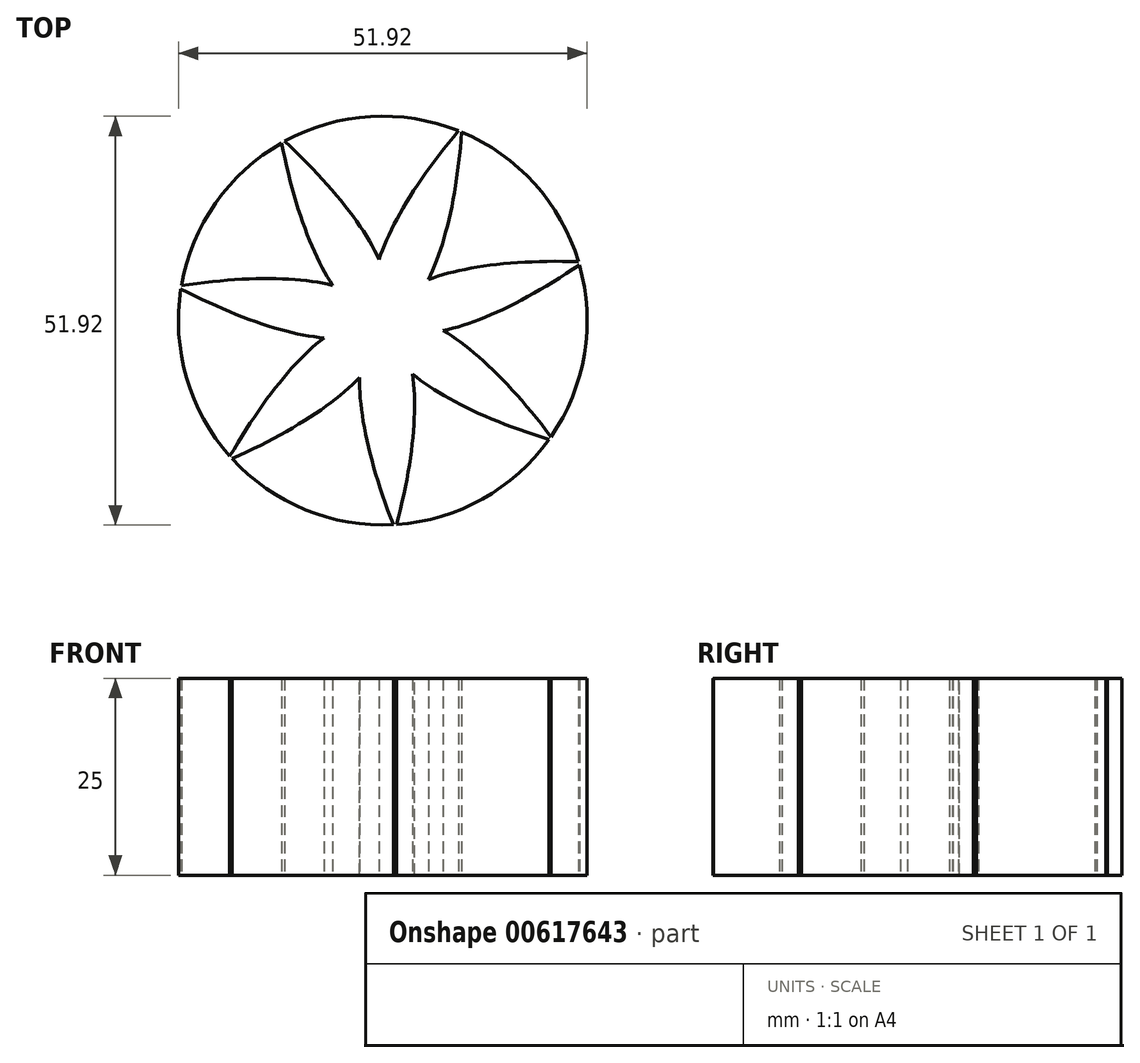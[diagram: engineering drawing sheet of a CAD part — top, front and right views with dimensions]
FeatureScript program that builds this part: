
annotation { "Feature Type Name" : "Feature", "Feature Type Description" : "" }
export const myFeature = defineFeature(function(context is Context, id is Id, definition is map)
    precondition{}
    {
        {
            var Q0;
            Q0=qCreatedBy(makeId("Top.planeOp"),FACE);
            var sketch = newSketch(context, id + "F0", { "sketchPlane" : qUnion([Q0])});
            skEllipse(sketch, "E0", {"center": v(-30.78, 21.65) * mm, "majorRadius": 37.63 * mm, "minorRadius": 12.4 * mm, "majorAxis": v(0.82, -0.58)});
            skEllipse(sketch, "E1.1.0", {"center": v(-36.12, -10.57) * mm, "majorRadius": 37.63 * mm, "minorRadius": 12.4 * mm, "majorAxis": v(0.96, 0.28)});
            skEllipse(sketch, "E1.2.0", {"center": v(-14.25, -34.83) * mm, "majorRadius": 37.63 * mm, "minorRadius": 12.4 * mm, "majorAxis": v(0.38, 0.93)});
            skEllipse(sketch, "E1.3.0", {"center": v(18.34, -32.86) * mm, "majorRadius": 37.63 * mm, "minorRadius": 12.4 * mm, "majorAxis": v(-0.49, 0.87)});
            skEllipse(sketch, "E1.4.0", {"center": v(37.13, -6.15) * mm, "majorRadius": 37.63 * mm, "minorRadius": 12.4 * mm, "majorAxis": v(-0.99, 0.16)});
            skEllipse(sketch, "E1.5.0", {"center": v(27.95, 25.2) * mm, "majorRadius": 37.63 * mm, "minorRadius": 12.4 * mm, "majorAxis": v(-0.74, -0.67)});
            skEllipse(sketch, "E1.6.0", {"center": v(-2.27, 37.56) * mm, "majorRadius": 37.63 * mm, "minorRadius": 12.4 * mm, "majorAxis": v(0.06, -1)});
            skPoint(sketch, "E1.center", {"position": v(0, 0) * mm});
            skCircle(sketch, "E2", {"center": v(0, 0) * mm, "radius": 25.96 * mm});
            skCircle(sketch, "E3", {"center": v(0, 0) * mm, "radius": 19.78 * mm});
            skSolve(sketch);
        }
        {
            var Q0;
            {var subQ0=sQuery(id+"F0.wireOp",EDGE,"E3");var subQ1=sQuery(id+"F0.wireOp",EDGE,"E1.1.0");var subQ2=makeQuery(id+"F0.imprint","INTERSECT",VERTEX,{"disambiguationData":[OD(0.0)],"derivedFrom":[subQ1,subQ0]});Q0=makeQuery(id+"F0.imprint","IMPRINT",FACE,{"disambiguationData":[TD([[makeQuery(id+"F0.imprint","IMPRINT",EDGE,{"disambiguationData":[TD([[subQ2,-1.0]])],"derivedFrom":subQ1}),-1.0]])]});}
            var Q1;
            {var subQ0=sQuery(id+"F0.wireOp",EDGE,"E2");var subQ1=sQuery(id+"F0.wireOp",EDGE,"E0");var subQ2=makeQuery(id+"F0.imprint","INTERSECT",VERTEX,{"disambiguationData":[OD(1.0)],"derivedFrom":[subQ1,subQ0]});Q1=makeQuery(id+"F0.imprint","IMPRINT",FACE,{"disambiguationData":[TD([[makeQuery(id+"F0.imprint","IMPRINT",EDGE,{"disambiguationData":[TD([[subQ2,-1.0]])],"derivedFrom":subQ1}),-1.0]])]});}
            var Q2;
            {var subQ0=sQuery(id+"F0.wireOp",EDGE,"E2");var subQ1=sQuery(id+"F0.wireOp",EDGE,"E1.1.0");var subQ2=makeQuery(id+"F0.imprint","INTERSECT",VERTEX,{"disambiguationData":[OD(1.0)],"derivedFrom":[subQ1,subQ0]});Q2=makeQuery(id+"F0.imprint","IMPRINT",FACE,{"disambiguationData":[TD([[makeQuery(id+"F0.imprint","IMPRINT",EDGE,{"disambiguationData":[TD([[subQ2,-1.0]])],"derivedFrom":subQ1}),-1.0]])]});}
            var Q3;
            {var subQ0=sQuery(id+"F0.wireOp",EDGE,"E2");var subQ1=sQuery(id+"F0.wireOp",EDGE,"E1.2.0");var subQ2=makeQuery(id+"F0.imprint","INTERSECT",VERTEX,{"disambiguationData":[OD(1.0)],"derivedFrom":[subQ1,subQ0]});Q3=makeQuery(id+"F0.imprint","IMPRINT",FACE,{"disambiguationData":[TD([[makeQuery(id+"F0.imprint","IMPRINT",EDGE,{"disambiguationData":[TD([[subQ2,-1.0]])],"derivedFrom":subQ1}),-1.0]])]});}
            var Q4;
            {var subQ0=sQuery(id+"F0.wireOp",EDGE,"E2");var subQ1=sQuery(id+"F0.wireOp",EDGE,"E1.3.0");var subQ2=makeQuery(id+"F0.imprint","INTERSECT",VERTEX,{"disambiguationData":[OD(1.0)],"derivedFrom":[subQ1,subQ0]});Q4=makeQuery(id+"F0.imprint","IMPRINT",FACE,{"disambiguationData":[TD([[makeQuery(id+"F0.imprint","IMPRINT",EDGE,{"disambiguationData":[TD([[subQ2,-1.0]])],"derivedFrom":subQ1}),-1.0]])]});}
            var Q5;
            {var subQ0=sQuery(id+"F0.wireOp",EDGE,"E2");var subQ1=sQuery(id+"F0.wireOp",EDGE,"E1.4.0");var subQ2=makeQuery(id+"F0.imprint","INTERSECT",VERTEX,{"disambiguationData":[OD(1.0)],"derivedFrom":[subQ1,subQ0]});Q5=makeQuery(id+"F0.imprint","IMPRINT",FACE,{"disambiguationData":[TD([[makeQuery(id+"F0.imprint","IMPRINT",EDGE,{"disambiguationData":[TD([[subQ2,-1.0]])],"derivedFrom":subQ1}),-1.0]])]});}
            var Q6;
            {var subQ0=sQuery(id+"F0.wireOp",EDGE,"E3");var subQ1=sQuery(id+"F0.wireOp",EDGE,"E0");var subQ2=makeQuery(id+"F0.imprint","INTERSECT",VERTEX,{"disambiguationData":[OD(0.0)],"derivedFrom":[subQ1,subQ0]});Q6=makeQuery(id+"F0.imprint","IMPRINT",FACE,{"disambiguationData":[TD([[makeQuery(id+"F0.imprint","IMPRINT",EDGE,{"disambiguationData":[TD([[subQ2,-1.0]])],"derivedFrom":subQ1}),-1.0]])]});}
            var Q7;
            {var subQ0=sQuery(id+"F0.wireOp",EDGE,"E1.6.0");var subQ1=sQuery(id+"F0.wireOp",EDGE,"E1.1.0");var subQ2=makeQuery(id+"F0.imprint","INTERSECT",VERTEX,{"derivedFrom":[subQ1,subQ0]});Q7=makeQuery(id+"F0.imprint","IMPRINT",FACE,{"disambiguationData":[TD([[makeQuery(id+"F0.imprint","IMPRINT",EDGE,{"disambiguationData":[TD([[subQ2,-1.0]])],"derivedFrom":subQ1}),-1.0]])]});}
            var Q8;
            {var subQ0=sQuery(id+"F0.wireOp",EDGE,"E3");var subQ1=sQuery(id+"F0.wireOp",EDGE,"E0");var subQ2=makeQuery(id+"F0.imprint","INTERSECT",VERTEX,{"disambiguationData":[OD(1.0)],"derivedFrom":[subQ1,subQ0]});Q8=makeQuery(id+"F0.imprint","IMPRINT",FACE,{"disambiguationData":[TD([[makeQuery(id+"F0.imprint","IMPRINT",EDGE,{"disambiguationData":[TD([[subQ2,-1.0]])],"derivedFrom":subQ1}),-1.0]])]});}
            var Q9;
            {var subQ0=sQuery(id+"F0.wireOp",EDGE,"E3");var subQ1=sQuery(id+"F0.wireOp",EDGE,"E1.1.0");var subQ2=makeQuery(id+"F0.imprint","INTERSECT",VERTEX,{"disambiguationData":[OD(1.0)],"derivedFrom":[subQ1,subQ0]});Q9=makeQuery(id+"F0.imprint","IMPRINT",FACE,{"disambiguationData":[TD([[makeQuery(id+"F0.imprint","IMPRINT",EDGE,{"disambiguationData":[TD([[subQ2,-1.0]])],"derivedFrom":subQ1}),-1.0]])]});}
            var Q10;
            {var subQ0=sQuery(id+"F0.wireOp",EDGE,"E3");var subQ1=sQuery(id+"F0.wireOp",EDGE,"E1.2.0");var subQ2=makeQuery(id+"F0.imprint","INTERSECT",VERTEX,{"disambiguationData":[OD(1.0)],"derivedFrom":[subQ1,subQ0]});Q10=makeQuery(id+"F0.imprint","IMPRINT",FACE,{"disambiguationData":[TD([[makeQuery(id+"F0.imprint","IMPRINT",EDGE,{"disambiguationData":[TD([[subQ2,-1.0]])],"derivedFrom":subQ1}),-1.0]])]});}
            var Q11;
            {var subQ0=sQuery(id+"F0.wireOp",EDGE,"E3");var subQ1=sQuery(id+"F0.wireOp",EDGE,"E1.3.0");var subQ2=makeQuery(id+"F0.imprint","INTERSECT",VERTEX,{"disambiguationData":[OD(1.0)],"derivedFrom":[subQ1,subQ0]});Q11=makeQuery(id+"F0.imprint","IMPRINT",FACE,{"disambiguationData":[TD([[makeQuery(id+"F0.imprint","IMPRINT",EDGE,{"disambiguationData":[TD([[subQ2,-1.0]])],"derivedFrom":subQ1}),-1.0]])]});}
            var Q12;
            {var subQ0=sQuery(id+"F0.wireOp",EDGE,"E3");var subQ1=sQuery(id+"F0.wireOp",EDGE,"E1.4.0");var subQ2=makeQuery(id+"F0.imprint","INTERSECT",VERTEX,{"disambiguationData":[OD(1.0)],"derivedFrom":[subQ1,subQ0]});Q12=makeQuery(id+"F0.imprint","IMPRINT",FACE,{"disambiguationData":[TD([[makeQuery(id+"F0.imprint","IMPRINT",EDGE,{"disambiguationData":[TD([[subQ2,-1.0]])],"derivedFrom":subQ1}),-1.0]])]});}
            var Q13;
            {var subQ0=sQuery(id+"F0.wireOp",EDGE,"E1.5.0");var subQ1=sQuery(id+"F0.wireOp",EDGE,"E0");var subQ2=makeQuery(id+"F0.imprint","INTERSECT",VERTEX,{"derivedFrom":[subQ1,subQ0]});Q13=makeQuery(id+"F0.imprint","IMPRINT",FACE,{"disambiguationData":[TD([[makeQuery(id+"F0.imprint","IMPRINT",EDGE,{"disambiguationData":[TD([[subQ2,-1.0]])],"derivedFrom":subQ1}),-1.0]])]});}
            extrude(context, id + "F1", {"entities" : qUnion([Q0, Q1, Q2, Q3, Q4, Q5, Q6, Q7, Q8, Q9, Q10, Q11, Q12, Q13]), "depth" : 25 * mm, "offsetDistance" : 25 * mm});
        }
        {
            var Q0;
            Q0=qCreatedBy(makeId("Top.planeOp"),FACE);
            var sketch = newSketch(context, id + "F2", { "sketchPlane" : qUnion([Q0])});
            skCircle(sketch, "E4", {"center": v(0, 0) * mm, "radius": 31.56 * mm});
            skSolve(sketch);
        }
        {
            var Q0;
            Q0=sQuery(id+"F2.wireOp",EDGE,"E4");
            var Q1;
            Q1=sQuery(id+"F0.wireOp",EDGE,"E2");
            extrude(context, id + "F3", {"bodyType" : ToolBodyType.SURFACE, "surfaceEntities" : qUnion([Q0, Q1]), "depth" : 25 * mm, "offsetDistance" : 25 * mm});
        }
    });
